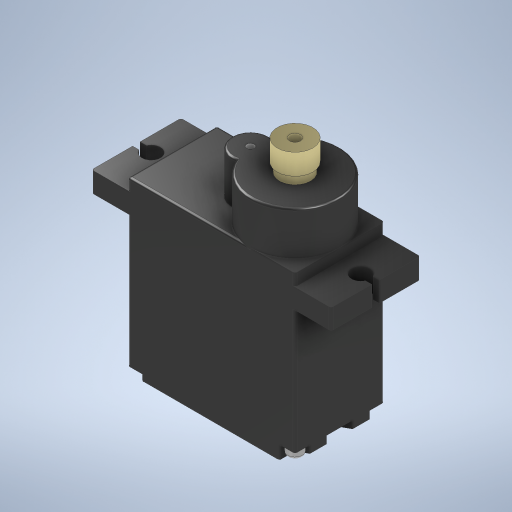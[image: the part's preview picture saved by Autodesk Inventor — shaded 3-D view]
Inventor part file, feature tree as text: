
AUTODESK INVENTOR PART (.ipt)
format: ipt  version: 2023.1 (Build 271208000, 208)  size: 585,728 bytes
history: native  units: mm
features: extrude x16, sketch x11, fillet x4, other x2, projected_geometry x2
ambient origin geometry x8: Origin, YZ Plane, XZ Plane, XY Plane, X Axis, Y Axis, Z Axis, Center Point
bodies: Body1 (feature_tree)
feature tree (35):
  other  "솔리드1"
  extrude  "돌출1"  Depth=22.5mm
  other  "작업 평면1"
  extrude  "돌출2"  Depth=12.0mm
  extrude  "돌출3"  Depth=23.0mm TaperAngle=0.0deg
  sketch  "스케치4"
  extrude  "돌출6"  [1 undecoded]
  extrude  "돌출7"  Depth=32.2mm
  fillet  "모깎기1"  Radius=12.0mm
  fillet  "모깎기2"  Radius=2.5mm
  sketch  "스케치5"
  extrude  "돌출8"  Depth=2.0mm
  extrude  "돌출9"  Depth=0.5mm
  extrude  "돌출10"  Depth=0.5mm
  extrude  "돌출11"  Depth=2.7mm TaperAngle=0.0deg
  fillet  "모깎기3"  Radius=1.0mm
  sketch  "스케치7"
  extrude  "돌출12"  Depth=1.5mm TaperAngle=0.0deg
  extrude  "돌출13"  Depth=5.0mm
  extrude  "돌출14"  Depth=6.0mm
  extrude  "돌출15"  Depth=5.0mm
  fillet  "모깎기4"  Radius=1.0mm
  extrude  "돌출16"  Depth=5.8mm TaperAngle=0.0deg
  sketch  "스케치12"
  sketch  "스케치14"
  extrude  "돌출18"  Depth=5.01mm TaperAngle=0.0deg
  extrude  "돌출19"  Depth=0.3mm
  sketch  "스케치15"
  sketch  "스케치16"
  sketch  "스케치1"
  sketch  "스케치2"
  sketch  "스케치3"
  projected_geometry  "투영된 루프1"
  projected_geometry  "투영된 루프2"
  sketch  "스케치6"
note: 1 required parameter value undecoded (feature->parameter linkage not recoverable at this tier; creation-order binding heuristic only, values carry confidence <= 0.55)
